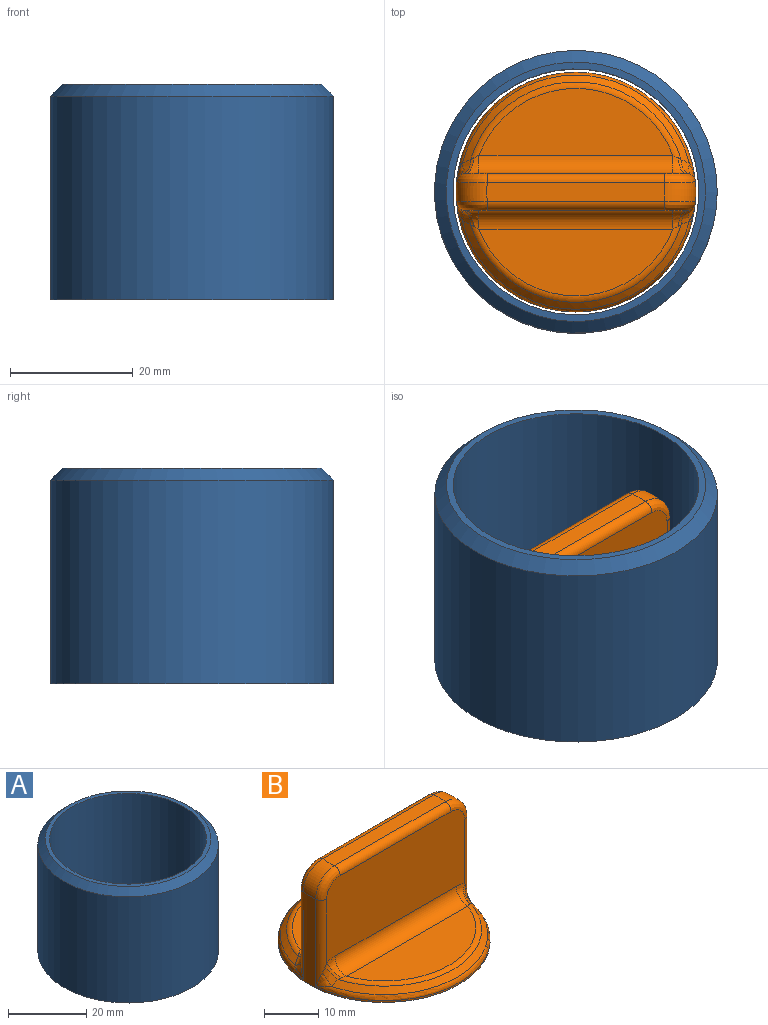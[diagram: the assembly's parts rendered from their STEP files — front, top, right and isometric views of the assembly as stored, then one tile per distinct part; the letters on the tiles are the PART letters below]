
ASSEMBLY  parts=2 mates=1
PART A: 5 faces, bbox 46x46x35 mm
  f0: cylinder r=20mm len=40mm, axis (0,0,-1), area 4398.2mm2, adj f2,f3
  f1: cylinder r=23mm len=46mm, axis (0,0,-1), area 4783.4mm2, adj f3,f4
  f2: plane 42.2x42.2mm, normal (0,0,1), area 142mm2, adj f0,f4
  f3: plane 46x46mm, normal (0,0,-1), area 405.3mm2, adj f0,f1
  f4: cone r=21.1mm half-angle=45deg, axis (0,0,-1), area 372.3mm2, adj f1,f2
PART B: 43 faces, bbox 42.1x42.2x25 mm
  f0: plane 31.55x10.88mm, normal (0,0,1), area 249.3mm2, adj f17,f29
  f1: cylinder r=19.5mm len=39mm, axis (0,0,-1), area 174.1mm2, adj f3,f7,f8,f13,f15,f16,f21,f22
  f2: plane 31.55x10.88mm, normal (0,0,1), area 249.3mm2, adj f24,f38
  f3: plane 39x39mm, normal (0,0,-1), area 1194.6mm2, adj f1
  f4: plane 35.88x17.99mm, normal (0,-1,0), area 623.2mm2, adj f18,f19,f20,f21,f22,f28,f29,f30
  f5: plane 35.88x17.99mm, normal (0,1,0), area 623.2mm2, adj f11,f12,f13,f14,f16,f37,f38,f39
  f6: plane 29x3mm, normal (0,0,1), area 86.8mm2, adj f7,f8,f12,f18
  f7: torus R=14.5mm, axis (0,0,1), area 25.8mm2, adj f1,f6,f11,f20
  f8: torus R=14.5mm, axis (0,0,1), area 25.8mm2, adj f1,f6,f14,f19
  f9: cone r=17.5mm half-angle=45deg, axis (0,0,-1), area 76.3mm2, adj f15,f24,f35,f41
  f10: cone r=17.5mm half-angle=45deg, axis (0,0,-1), area 76.3mm2, adj f17,f23,f26,f32
  f11: bspline ~6.14x6.12mm, area 15.9mm2, adj f5,f7,f12,f13
  f12: cylinder r=1.5mm len=28.84mm, axis (1,0,0), area 68mm2, adj f5,f6,f11,f14
  f13: cylinder r=1.5mm len=19.62mm, axis (0,0,-1), area 37.8mm2, adj f1,f5,f11,f40,f41,f42
  f14: bspline ~6.14x6.12mm, area 15.9mm2, adj f5,f8,f12,f16
  f15: torus R=18mm, axis (0,0,1), area 64.1mm2, adj f1,f9,f34,f42
  f16: cylinder r=1.5mm len=19.62mm, axis (0,0,-1), area 37.8mm2, adj f1,f5,f14,f34,f35,f36
  f17: torus R=16.88mm, axis (0,0,1), area 51mm2, adj f0,f10,f27,f28,f30,f31
  f18: cylinder r=1.5mm len=28.84mm, axis (-1,0,0), area 68mm2, adj f4,f6,f19,f20
  f19: bspline ~6.12x5.3mm, area 15.9mm2, adj f4,f8,f18,f21
  f20: bspline ~6.14x6.12mm, area 15.9mm2, adj f4,f7,f18,f22
  f21: cylinder r=1.5mm len=19.62mm, axis (0,0,-1), area 37.8mm2, adj f1,f4,f19,f25,f26,f27
  f22: cylinder r=1.5mm len=19.62mm, axis (0,0,-1), area 37.8mm2, adj f1,f4,f20,f31,f32,f33
  f23: torus R=18mm, axis (0,0,1), area 64.1mm2, adj f1,f10,f25,f33
  f24: torus R=16.88mm, axis (0,0,1), area 51mm2, adj f2,f9,f36,f37,f39,f40
  f25: bspline ~3.73x3.54mm, area 4.4mm2, adj f21,f23,f26
  f26: bspline ~4.41x2.8mm, area 4.6mm2, adj f10,f21,f25,f27
  f27: bspline ~3.5x2.81mm, area 2.3mm2, adj f17,f21,f26,f28
  f28: bspline ~4.13x3.32mm, area 6.3mm2, adj f4,f17,f27,f29
  f29: cylinder r=3mm len=31.55mm, axis (-1,0,0), area 148.7mm2, adj f0,f4,f28,f30
  f30: bspline ~4.21x3.34mm, area 6.3mm2, adj f4,f17,f29,f31
  f31: bspline ~3.5x2.81mm, area 2.3mm2, adj f17,f22,f30,f32
  f32: bspline ~4.79x3.09mm, area 4.6mm2, adj f10,f22,f31,f33
  f33: bspline ~3.73x3.54mm, area 4.4mm2, adj f22,f23,f32
  f34: bspline ~3.73x3.54mm, area 4.4mm2, adj f15,f16,f35
  f35: bspline ~4.79x3.09mm, area 4.6mm2, adj f9,f16,f34,f36
  f36: bspline ~3.5x2.81mm, area 2.3mm2, adj f16,f24,f35,f37
  f37: bspline ~4.21x3.34mm, area 6.3mm2, adj f5,f24,f36,f38
  f38: cylinder r=3mm len=31.55mm, axis (1,0,0), area 148.7mm2, adj f2,f5,f37,f39
  f39: bspline ~3.82x3.32mm, area 6.3mm2, adj f5,f24,f38,f40
  f40: bspline ~3.5x2.81mm, area 2.3mm2, adj f13,f24,f39,f41
  f41: bspline ~4.41x2.8mm, area 4.6mm2, adj f9,f13,f40,f42
  f42: bspline ~3.73x3.54mm, area 4.4mm2, adj f13,f15,f41
PLACE A t=(4.89,0.92,-5.98)mm
PLACE B t=(4.89,0.92,-5.74)mm
MATE cylindrical B.f1 <-> A.f0  axis (0,0,-1) through (4.89,0.92,-5.74)mm
